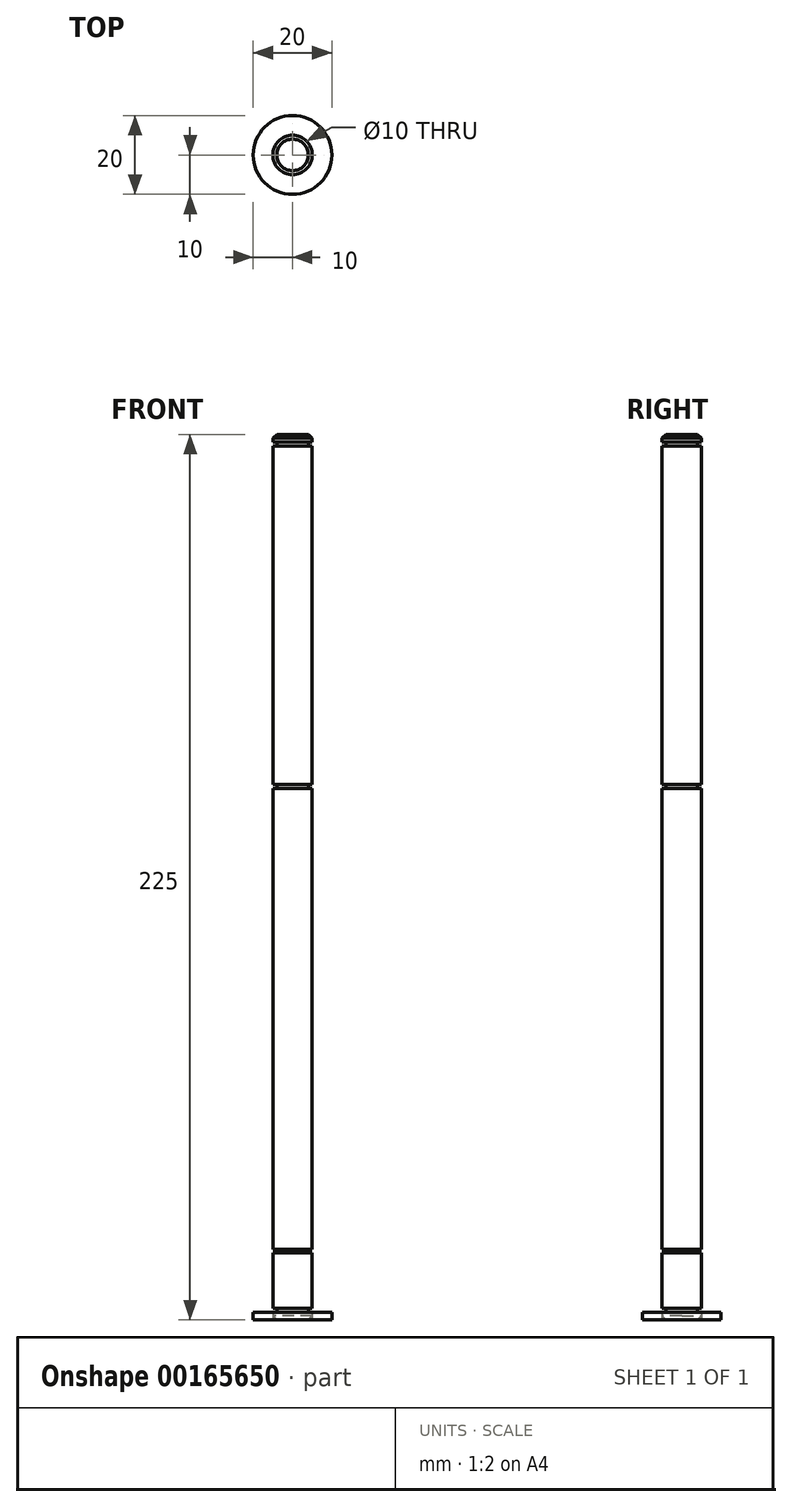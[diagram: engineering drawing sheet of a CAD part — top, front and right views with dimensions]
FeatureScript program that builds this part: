
annotation { "Feature Type Name" : "Feature", "Feature Type Description" : "" }
export const myFeature = defineFeature(function(context is Context, id is Id, definition is map)
    precondition{}
    {
        {
            var Q0;
            Q0=qCreatedBy(makeId("Top.planeOp"),FACE);
            var sketch = newSketch(context, id + "F0", { "sketchPlane" : qUnion([Q0])});
            skCircle(sketch, "E0", {"center": v(0, 0) * mm, "radius": 5 * mm});
            skSolve(sketch);
        }
        {
            var Q0;
            Q0=makeQuery(id+"F0.imprint","IMPRINT",FACE,{"disambiguationData":[TD([[makeQuery(id+"F0.imprint","IMPRINT",EDGE,{"derivedFrom":sQuery(id+"F0.wireOp",EDGE,"E0")}),1.0]])]});
            extrude(context, id + "F1", {"entities" : qUnion([Q0]), "depth" : 225 * mm, "offsetDistance" : 25 * mm});
        }
        {
            var Q0;
            Q0=makeQuery(id+"F1.opExtrude","CAP_EDGE",EDGE,{"disambiguationData":[OSD([sQuery(id+"F0.wireOp",EDGE,"E0")])],"isStart":false});
            var Q1;
            Q1=makeQuery(id+"F1.opExtrude","CAP_EDGE",EDGE,{"disambiguationData":[OSD([sQuery(id+"F0.wireOp",EDGE,"E0")])],"isStart":true});
            chamfer(context, id + "F2", {"entities" : qUnion([Q0, Q1]), "width" : 1 * mm, "tangentPropagation" : true});
        }
        {
            var Q0;
            Q0=makeQuery(id+"F1.opExtrude","CAP_FACE",FACE,{"disambiguationData":[OSD([sQuery(id+"F0.wireOp",EDGE,"E0")])],"isStart":true});
            cPlane(context, id + "F3", {"entities" : qUnion([Q0]), "cplaneType" : CPlaneType.OFFSET, "offset" : 2 * mm, "oppositeDirection" : true, "width" : 150 * mm, "height" : 150 * mm});
        }
        {
            var Q0;
            Q0=qCreatedBy(id+"F3.planeOp",FACE);
            var sketch = newSketch(context, id + "F4", { "sketchPlane" : qUnion([Q0])});
            skCircle(sketch, "E1", {"center": v(0, 0) * mm, "radius": 5 * mm});
            skCircle(sketch, "E2.0", {"center": v(0, 0) * mm, "radius": 4 * mm});
            skSolve(sketch);
        }
        {
            var Q0;
            Q0=makeQuery(id+"F4.imprint","IMPRINT",FACE,{"disambiguationData":[TD([[makeQuery(id+"F4.imprint","IMPRINT",EDGE,{"derivedFrom":sQuery(id+"F4.wireOp",EDGE,"E1")}),1.0]])]});
            extrude(context, id + "F5", {"entities" : qUnion([Q0]), "operationType" : NewBodyOperationType.REMOVE, "oppositeDirection" : true, "depth" : 1 * mm, "offsetDistance" : 25 * mm});
        }
        {
            var Q0;
            Q0=makeQuery(id+"F1.opExtrude","CAP_FACE",FACE,{"disambiguationData":[OSD([sQuery(id+"F0.wireOp",EDGE,"E0")])],"isStart":false});
            cPlane(context, id + "F6", {"entities" : qUnion([Q0]), "cplaneType" : CPlaneType.OFFSET, "offset" : 2 * mm, "oppositeDirection" : true, "width" : 150 * mm, "height" : 150 * mm});
        }
        {
            var Q0;
            Q0=qCreatedBy(id+"F6.planeOp",FACE);
            var sketch = newSketch(context, id + "F7", { "sketchPlane" : qUnion([Q0])});
            skCircle(sketch, "E3", {"center": v(0, 0) * mm, "radius": 5 * mm});
            skCircle(sketch, "E4.0", {"center": v(0, 0) * mm, "radius": 4 * mm});
            skSolve(sketch);
        }
        {
            var Q0;
            Q0 = qSketchRegion(id + "F7", true);
            extrude(context, id + "F8", {"entities" : qUnion([Q0]), "operationType" : NewBodyOperationType.REMOVE, "oppositeDirection" : true, "depth" : 1 * mm, "offsetDistance" : 25 * mm});
        }
        {
            var Q0;
            Q0=makeQuery(id+"F1.opExtrude","CAP_FACE",FACE,{"disambiguationData":[OSD([sQuery(id+"F0.wireOp",EDGE,"E0")])],"isStart":true});
            cPlane(context, id + "F9", {"entities" : qUnion([Q0]), "cplaneType" : CPlaneType.OFFSET, "offset" : 17 * mm, "oppositeDirection" : true, "width" : 150 * mm, "height" : 150 * mm});
        }
        {
            var Q0;
            Q0=qCreatedBy(id+"F9.planeOp",FACE);
            var sketch = newSketch(context, id + "F10", { "sketchPlane" : qUnion([Q0])});
            skCircle(sketch, "E5", {"center": v(0, 0) * mm, "radius": 5 * mm});
            skCircle(sketch, "E6.0", {"center": v(0, 0) * mm, "radius": 4 * mm});
            skSolve(sketch);
        }
        {
            var Q0;
            Q0 = qSketchRegion(id + "F10", true);
            extrude(context, id + "F11", {"entities" : qUnion([Q0]), "operationType" : NewBodyOperationType.REMOVE, "oppositeDirection" : true, "depth" : 1 * mm, "offsetDistance" : 25 * mm});
        }
        {
            var Q0;
            Q0=makeQuery(id+"F1.opExtrude","CAP_FACE",FACE,{"disambiguationData":[OSD([sQuery(id+"F0.wireOp",EDGE,"E0")])],"isStart":true});
            cPlane(context, id + "F12", {"entities" : qUnion([Q0]), "cplaneType" : CPlaneType.OFFSET, "offset" : 135 * mm, "oppositeDirection" : true, "width" : 150 * mm, "height" : 150 * mm});
        }
        {
            var Q0;
            Q0=qCreatedBy(id+"F12.planeOp",FACE);
            var sketch = newSketch(context, id + "F13", { "sketchPlane" : qUnion([Q0])});
            skCircle(sketch, "E7", {"center": v(0, 0) * mm, "radius": 5 * mm});
            skCircle(sketch, "E8.0", {"center": v(0, 0) * mm, "radius": 4 * mm});
            skSolve(sketch);
        }
        {
            var Q0;
            Q0 = qSketchRegion(id + "F13", true);
            extrude(context, id + "F14", {"entities" : qUnion([Q0]), "operationType" : NewBodyOperationType.REMOVE, "oppositeDirection" : true, "depth" : 1 * mm, "offsetDistance" : 25 * mm});
        }
        {
            var Q0;
            Q0=qCreatedBy(makeId("Top.planeOp"),FACE);
            var sketch = newSketch(context, id + "F15", { "sketchPlane" : qUnion([Q0])});
            skCircle(sketch, "E9", {"center": v(0, 0) * mm, "radius": 5 * mm});
            skCircle(sketch, "E10", {"center": v(0, 0) * mm, "radius": 10 * mm});
            skSolve(sketch);
        }
        {
            var Q0;
            Q0=makeQuery(id+"F15.imprint","IMPRINT",FACE,{"disambiguationData":[TD([[makeQuery(id+"F15.imprint","IMPRINT",EDGE,{"derivedFrom":sQuery(id+"F15.wireOp",EDGE,"E9")}),-1.0]])]});
            extrude(context, id + "F16", {"entities" : qUnion([Q0]), "depth" : 2 * mm, "offsetDistance" : 25 * mm});
        }
    });
